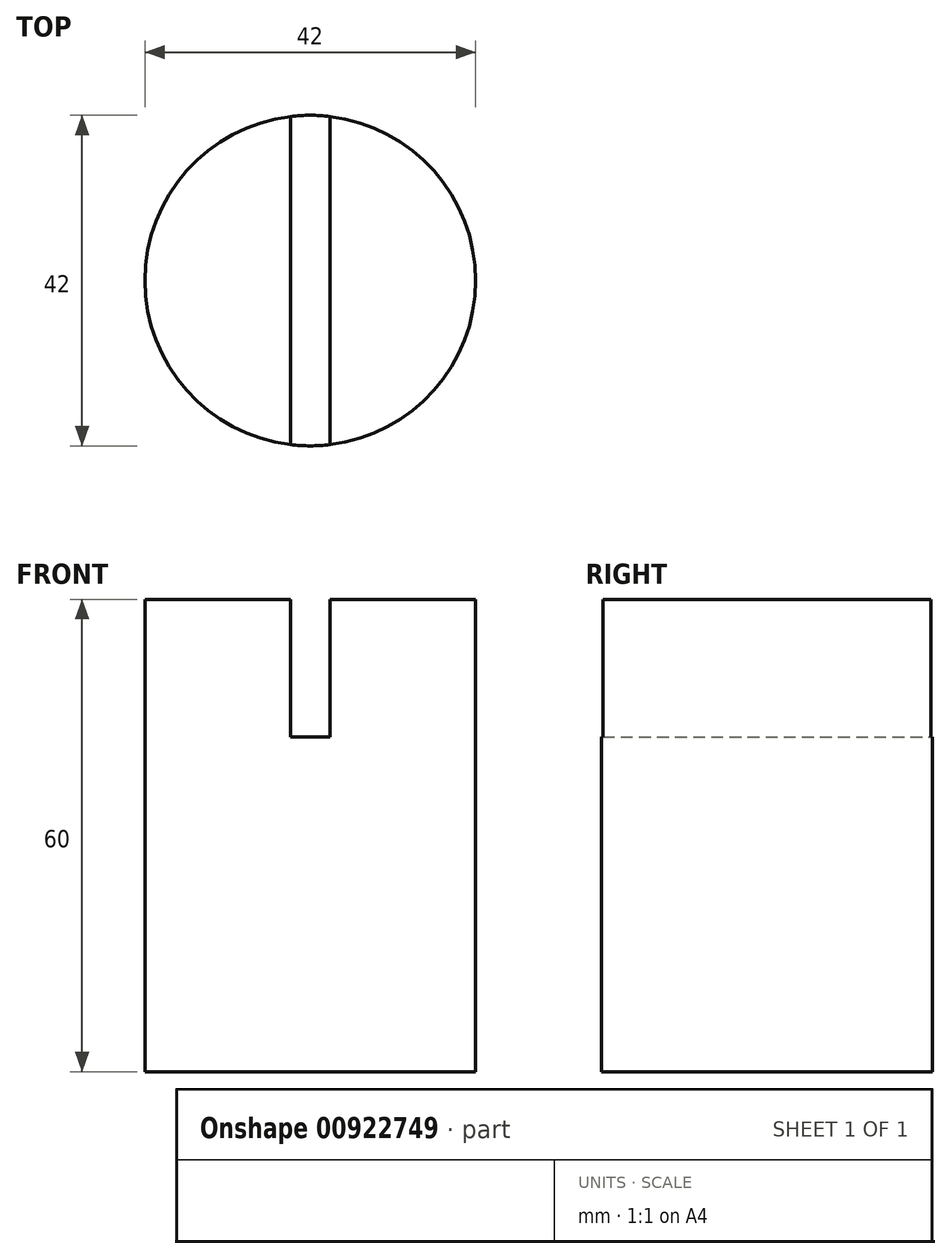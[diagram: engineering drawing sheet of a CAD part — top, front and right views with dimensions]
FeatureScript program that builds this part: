
annotation { "Feature Type Name" : "Feature", "Feature Type Description" : "" }
export const myFeature = defineFeature(function(context is Context, id is Id, definition is map)
    precondition{}
    {
        {
            var Q0;
            Q0=qCreatedBy(makeId("Top.planeOp"),FACE);
            var sketch = newSketch(context, id + "F0", { "sketchPlane" : qUnion([Q0])});
            skCircle(sketch, "E0", {"center": v(0, 0) * mm, "radius": 21 * mm});
            skSolve(sketch);
        }
        {
            var Q0;
            Q0 = qSketchRegion(id + "F0", true);
            extrude(context, id + "F1", {"entities" : qUnion([Q0]), "oppositeDirection" : true, "depth" : 60 * mm, "offsetDistance" : 25 * mm});
        }
        {
            var Q0;
            Q0=qCreatedBy(makeId("Front.planeOp"),FACE);
            var sketch = newSketch(context, id + "F2", { "sketchPlane" : qUnion([Q0])});
            skLineSegment(sketch, "E1.bottom", {"start": v(-2.5, 17.5) * mm, "end": v(2.5, 17.5) * mm});
            skLineSegment(sketch, "E1.top", {"start": v(-2.5, -17.5) * mm, "end": v(2.5, -17.5) * mm});
            skLineSegment(sketch, "E1.left", {"start": v(-2.5, 17.5) * mm, "end": v(-2.5, -17.5) * mm});
            skLineSegment(sketch, "E1.right", {"start": v(2.5, 17.5) * mm, "end": v(2.5, -17.5) * mm});
            skPoint(sketch, "E1.middle", {"position": v(0, 0) * mm});
            skSolve(sketch);
        }
        {
            var Q0;
            Q0 = qSketchRegion(id + "F2", true);
            extrude(context, id + "F3", {"entities" : qUnion([Q0]), "operationType" : NewBodyOperationType.REMOVE, "endBound" : BoundingType.THROUGH_ALL, "depth" : 25 * mm, "offsetDistance" : 25 * mm, "hasSecondDirection" : true, "secondDirectionBound" : SecondDirectionBoundingType.THROUGH_ALL, "secondDirectionOppositeDirection" : true, "secondDirectionDepth" : 25 * mm});
        }
    });
